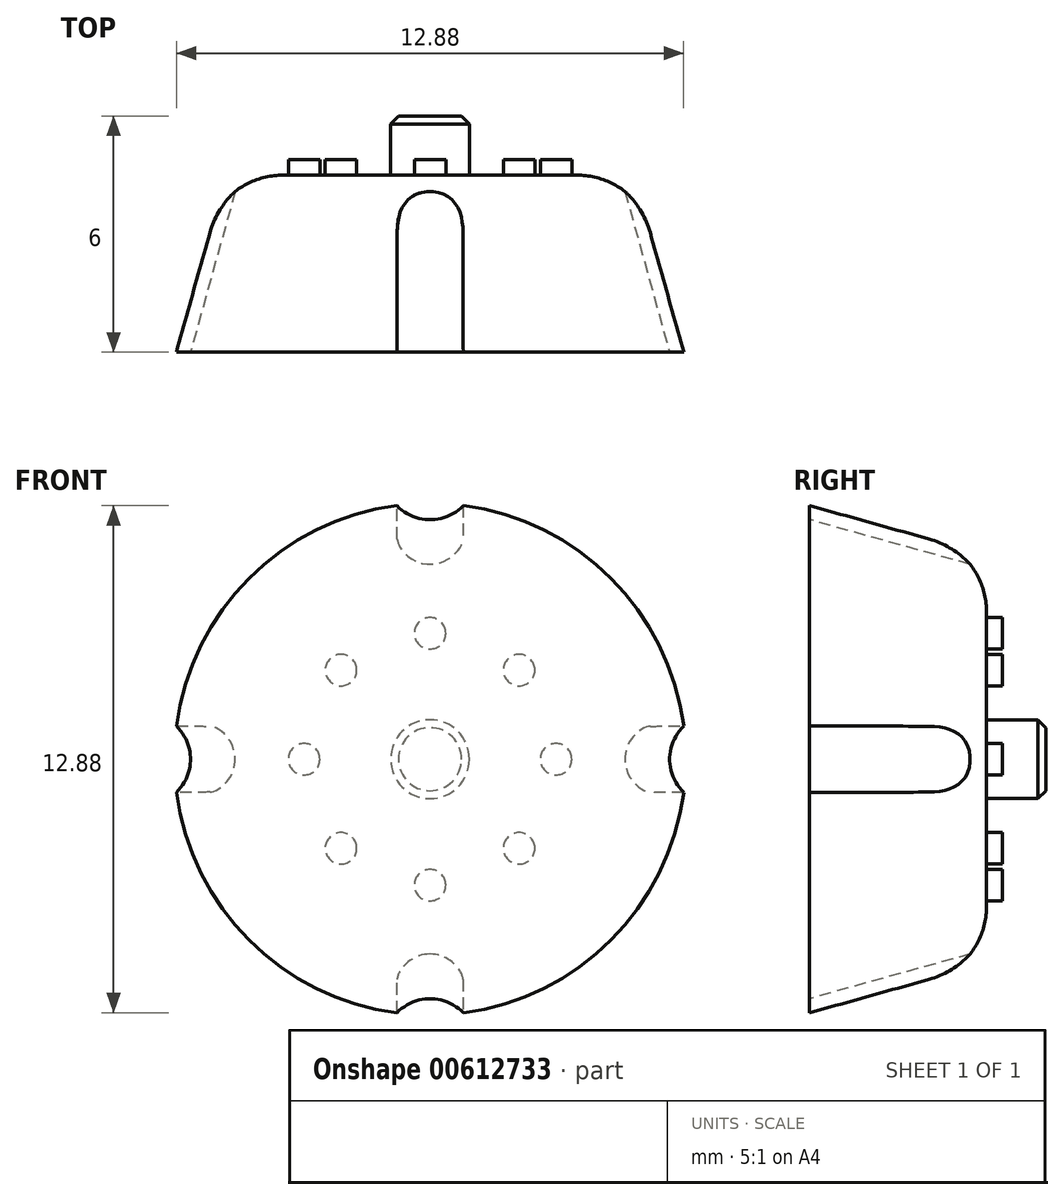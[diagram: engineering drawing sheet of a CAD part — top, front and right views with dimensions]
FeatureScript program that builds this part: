
annotation { "Feature Type Name" : "Feature", "Feature Type Description" : "" }
export const myFeature = defineFeature(function(context is Context, id is Id, definition is map)
    precondition{}
    {
        {
            var Q0;
            Q0=qCreatedBy(makeId("Top.planeOp"),FACE);
            var sketch = newSketch(context, id + "F0", { "sketchPlane" : qUnion([Q0])});
            skLineSegment(sketch, "E0", {"start": v(0, 0) * mm, "end": v(0, 26.8) * mm, "construction": true});
            skLineSegment(sketch, "E1", {"start": v(0, 0) * mm, "end": v(-6.5, 0) * mm});
            skLineSegment(sketch, "E2", {"start": v(-6.5, 0) * mm, "end": v(-5.66, 3.04) * mm});
            skLineSegment(sketch, "E3", {"start": v(-3.73, 4.5) * mm, "end": v(0, 4.5) * mm});
            skLineSegment(sketch, "E4", {"start": v(0, 4.5) * mm, "end": v(0, 0) * mm});
            skPoint(sketch, "E5.visualSharp", {"position": v(-5.25, 4.5) * mm});
            skArc(sketch, "E5.filletArc", {"start": v(-3.73, 4.5) * mm, "mid": v(-4.94, 4.1) * mm, "end": v(-5.66, 3.04) * mm});
            skSolve(sketch);
        }
        {
            var Q0;
            Q0=qSketchRegion(id+"F0",true);
            var Q1;
            Q1=sQuery(id+"F0.wireOp",EDGE,"E0");
            revolve(context, id + "F1", {"entities" : qUnion([Q0]), "axis" : qUnion([Q1]), "revolveType" : RevolveType.FULL});
        }
        {
            var Q0;
            Q0=makeQuery(id+"F1.opRevolve","SWEPT_FACE",FACE,{"disambiguationData":[OSD([sQuery(id+"F0.wireOp",EDGE,"E3")])]});
            var sketch = newSketch(context, id + "F2", { "sketchPlane" : qUnion([Q0])});
            skCircle(sketch, "E6", {"center": v(0, 0) * mm, "radius": 1 * mm});
            skSolve(sketch);
        }
        {
            var Q0;
            Q0=qSketchRegion(id+"F2",true);
            extrude(context, id + "F3", {"entities" : qUnion([Q0]), "operationType" : NewBodyOperationType.ADD, "depth" : 1.5 * mm, "offsetDistance" : 25 * mm});
        }
        {
            var Q0;
            Q0=makeQuery(id+"F3.opExtrude","CAP_FACE",FACE,{"disambiguationData":[OSD([sQuery(id+"F2.wireOp",EDGE,"E6")])],"isStart":false});
            chamfer(context, id + "F4", {"entities" : qUnion([Q0]), "width" : 0.2 * mm, "tangentPropagation" : true});
        }
        {
            var Q0;
            Q0=makeQuery(id+"F1.opRevolve","SWEPT_FACE",FACE,{"disambiguationData":[OSD([sQuery(id+"F0.wireOp",EDGE,"E3")])]});
            var sketch = newSketch(context, id + "F5", { "sketchPlane" : qUnion([Q0])});
            skCircle(sketch, "E7", {"center": v(0, 0) * mm, "radius": 3.2 * mm, "construction": true});
            skCircle(sketch, "E8", {"center": v(0, 3.2) * mm, "radius": 0.4 * mm});
            skCircle(sketch, "E9", {"center": v(3.2, 0) * mm, "radius": 0.4 * mm});
            skCircle(sketch, "E10", {"center": v(0, -3.2) * mm, "radius": 0.4 * mm});
            skCircle(sketch, "E11", {"center": v(-3.2, 0) * mm, "radius": 0.4 * mm});
            skLineSegment(sketch, "E12", {"start": v(-6.52, 6.52) * mm, "end": v(7.02, -7.02) * mm, "construction": true});
            skLineSegment(sketch, "E13", {"start": v(-6.76, -6.76) * mm, "end": v(6.87, 6.87) * mm, "construction": true});
            skCircle(sketch, "E14", {"center": v(-2.26, 2.26) * mm, "radius": 0.4 * mm});
            skCircle(sketch, "E15", {"center": v(2.26, 2.26) * mm, "radius": 0.4 * mm});
            skCircle(sketch, "E16", {"center": v(2.26, -2.26) * mm, "radius": 0.4 * mm});
            skCircle(sketch, "E17", {"center": v(-2.26, -2.26) * mm, "radius": 0.4 * mm});
            skSolve(sketch);
        }
        {
            var Q0;
            Q0=qSketchRegion(id+"F5",true);
            extrude(context, id + "F6", {"entities" : qUnion([Q0]), "operationType" : NewBodyOperationType.ADD, "depth" : 0.4 * mm, "offsetDistance" : 25 * mm});
        }
        {
            var Q0;
            Q0=qCreatedBy(makeId("Right.planeOp"),FACE);
            var sketch = newSketch(context, id + "F7", { "sketchPlane" : qUnion([Q0])});
            skLineSegment(sketch, "E18", {"start": v(-1.98, 7.88) * mm, "end": v(11.94, 4.01) * mm, "construction": true});
            skLineSegment(sketch, "E19", {"start": v(-0.39, 6.6) * mm, "end": v(3.82, 5.44) * mm, "construction": true});
            skLineSegment(sketch, "E20", {"start": v(3.82, -5.44) * mm, "end": v(-0.39, -6.6) * mm, "construction": true});
            skLineSegment(sketch, "E21.0", {"start": v(3.04, -5.66) * mm, "end": v(3.04, 5.66) * mm, "construction": true});
            skLineSegment(sketch, "E22", {"start": v(-1.07, 7.63) * mm, "end": v(-0.75, 8.78) * mm});
            skLineSegment(sketch, "E23", {"start": v(-0.75, 8.78) * mm, "end": v(6.34, 6.82) * mm});
            skLineSegment(sketch, "E24", {"start": v(6.34, 6.82) * mm, "end": v(6.01, 5.66) * mm});
            skLineSegment(sketch, "E25", {"start": v(6.01, 5.66) * mm, "end": v(-1.07, 7.63) * mm});
            skSolve(sketch);
        }
        {
            var Q0;
            Q0=qSketchRegion(id+"F7",true);
            var Q1;
            Q1=sQuery(id+"F7.wireOp",EDGE,"E18");
            revolve(context, id + "F8", {"entities" : qUnion([Q0]), "axis" : qUnion([Q1]), "revolveType" : RevolveType.FULL});
        }
        {
            var Q0;
            Q0=makeQuery(id+"F8.opRevolve","SWEPT_BODY",BODY,{"disambiguationData":[OSD([sQuery(id+"F7.wireOp",EDGE,"E22"),sQuery(id+"F7.wireOp",EDGE,"E23"),sQuery(id+"F7.wireOp",EDGE,"E24"),sQuery(id+"F7.wireOp",EDGE,"E25")])]});
            var Q1;
            {var subQ0=sQuery(id+"F2.wireOp",EDGE,"E6");Q1=makeQuery(id+"F4.opChamfer","BLEND_EDGE",EDGE,{"blendedFrom":[makeQuery(id+"F3.opExtrude","CAP_EDGE",EDGE,{"disambiguationData":[OSD([subQ0])],"isStart":false}),makeQuery(id+"F3.opExtrude","SWEPT_FACE",FACE,{"disambiguationData":[OSD([subQ0])]})],"blendedInto":[makeQuery(id+"F3.opExtrude","SWEPT_FACE",FACE,{"disambiguationData":[OSD([subQ0])]})]});}
            circularPattern(context, id + "F9", {"entities" : qUnion([Q0]), "axis" : qUnion([Q1]), "angle" : 360 * degree, "instanceCount" : 4, "equalSpace" : true});
        }
        {
            var Q0;
            Q0=makeQuery(id+"F8.opRevolve","SWEPT_BODY",BODY,{"disambiguationData":[OSD([sQuery(id+"F7.wireOp",EDGE,"E22"),sQuery(id+"F7.wireOp",EDGE,"E23"),sQuery(id+"F7.wireOp",EDGE,"E24"),sQuery(id+"F7.wireOp",EDGE,"E25")])]});
            var Q1;
            Q1=makeQuery(id+"F9.opPattern","COPY",BODY,{"derivedFrom":makeQuery(id+"F8.opRevolve","SWEPT_BODY",BODY,{"disambiguationData":[OSD([sQuery(id+"F7.wireOp",EDGE,"E22"),sQuery(id+"F7.wireOp",EDGE,"E23"),sQuery(id+"F7.wireOp",EDGE,"E24"),sQuery(id+"F7.wireOp",EDGE,"E25")])]}),"instanceName":"1"});
            var Q2;
            Q2=makeQuery(id+"F9.opPattern","COPY",BODY,{"derivedFrom":makeQuery(id+"F8.opRevolve","SWEPT_BODY",BODY,{"disambiguationData":[OSD([sQuery(id+"F7.wireOp",EDGE,"E22"),sQuery(id+"F7.wireOp",EDGE,"E23"),sQuery(id+"F7.wireOp",EDGE,"E24"),sQuery(id+"F7.wireOp",EDGE,"E25")])]}),"instanceName":"2"});
            var Q3;
            Q3=makeQuery(id+"F9.opPattern","COPY",BODY,{"derivedFrom":makeQuery(id+"F8.opRevolve","SWEPT_BODY",BODY,{"disambiguationData":[OSD([sQuery(id+"F7.wireOp",EDGE,"E22"),sQuery(id+"F7.wireOp",EDGE,"E23"),sQuery(id+"F7.wireOp",EDGE,"E24"),sQuery(id+"F7.wireOp",EDGE,"E25")])]}),"instanceName":"3"});
            var Q4;
            Q4=makeQuery(id+"F1.opRevolve","SWEPT_BODY",BODY,{"disambiguationData":[OSD([sQuery(id+"F0.wireOp",EDGE,"E1"),sQuery(id+"F0.wireOp",EDGE,"E2"),sQuery(id+"F0.wireOp",EDGE,"E3"),sQuery(id+"F0.wireOp",EDGE,"E4"),sQuery(id+"F0.wireOp",EDGE,"E5.filletArc")])]});
            booleanBodies(context, id + "F10", {"operationType" : BooleanOperationType.SUBTRACTION, "tools" : qUnion([Q0, Q1, Q2, Q3]), "targets" : qUnion([Q4])});
        }
    });
